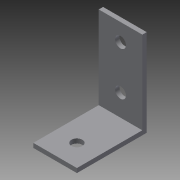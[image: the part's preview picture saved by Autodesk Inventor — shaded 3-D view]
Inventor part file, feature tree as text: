
AUTODESK INVENTOR PART (.ipt)
format: ipt  version: 2015 (Build 190159000, 159)  size: 104,448 bytes
history: native  units: in
note: dims shown in document units (in); Inventor stores cm internally (conversion verified against a paired STEP export)
features: sketch x4, extrude x3, hole x1
ambient origin geometry x8: Origin, YZ Plane, XZ Plane, XY Plane, X Axis, Y Axis, Z Axis, Center Point
bodies: Solid1 (feature_tree)
feature tree (8):
  extrude  "Extrusion1"  Depth=0.5in
  hole  "Hole1"  [1 undecoded]
  extrude  "Extrusion2"  Depth=0.5in
  extrude  "Extrusion3"  Depth=0.05in
  sketch  "Sketch1"  dims[d0=1.0in d1=0.5in]
  sketch  "Sketch2"  dims[d2=0.05in d3=0.0in d4=0.25in]
  sketch  "Sketch3"  dims[d5=0.3in d6=0.5in]
  sketch  "Sketch4"  dims[d7=0.125in d8=0.75in d9=0.375in d10=0.25in d11=0.5635in d12=1.0in d13=0.8108in d14=0.05in d15=0.75in d16=0.0in d17=0.25in d18=0.125in d19=0.25in d20=0.75in d21=0.0in]
note: 1 required parameter value undecoded (feature->parameter linkage not recoverable at this tier; creation-order binding heuristic only, values carry confidence <= 0.55)
